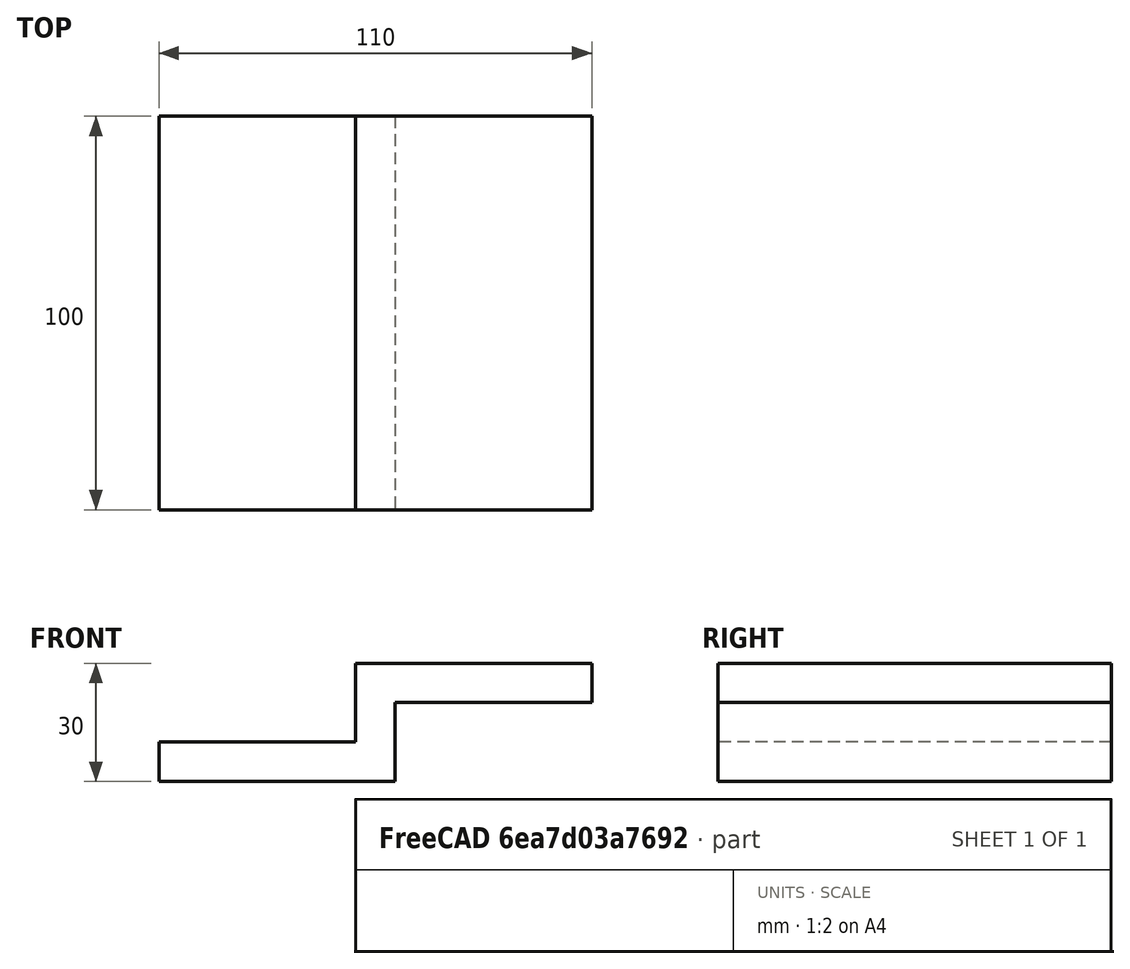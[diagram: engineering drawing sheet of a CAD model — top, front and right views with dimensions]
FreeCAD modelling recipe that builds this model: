
FCSTD DOCUMENT  (FreeCAD 0.17R13327 (Git))
Label: Z
License: All rights reserved
LicenseURL: http://en.wikipedia.org/wiki/All_rights_reserved
objects: Sketcher::SketchObject×1, PartDesign::Pad×1
note: 3 computed .brp shape members not serialized (recipe doc carries the construction recipe); baked Part::Feature solids carry a one-line shape summary decoded from their .brp

FEATURE [Sketcher::SketchObject] Sketch
  MapMode = 5
  Placement = pos=(0,0,0) rot=(1,0,0;1.5708rad)
  sketch-geometry (8):
    g0: LineSegment StartX=0 StartY=0 StartZ=0 EndX=60 EndY=0 EndZ=0
    g1: LineSegment StartX=60 StartY=0 StartZ=0 EndX=60 EndY=20 EndZ=0
    g2: LineSegment StartX=60 StartY=20 StartZ=0 EndX=110 EndY=20 EndZ=0
    g3: LineSegment StartX=110 StartY=20 StartZ=0 EndX=110 EndY=30 EndZ=0
    g4: LineSegment StartX=110 StartY=30 StartZ=0 EndX=50 EndY=30 EndZ=0
    g5: LineSegment StartX=50 StartY=30 StartZ=0 EndX=50 EndY=10 EndZ=0
    g6: LineSegment StartX=50 StartY=10 StartZ=0 EndX=0 EndY=10 EndZ=0
    g7: LineSegment StartX=0 StartY=10 StartZ=0 EndX=0 EndY=0 EndZ=0
  constraints (17):
    c: PointOnObject(g0,g-2)
    c: PointOnObject(g0,g-1)
    c: Horizontal(g0)
    c: Coincident(g0,g1)
    c: Vertical(g1)
    c: Coincident(g1,g2)
    c: Horizontal(g2)
    c: Coincident(g2,g3)
    c: Vertical(g3)
    c: Coincident(g3,g4)
    c: Horizontal(g4)
    c: Coincident(g4,g5)
    c: Vertical(g5)
    c: Horizontal(g6)
    c: Coincident(g6,g7)
    c: Coincident(g5,g6)
    c: Coincident(g-1,g7)
FEATURE [PartDesign::Pad] Pad
  Length = 100
  Length2 = 100
  Placement = pos=(0,0,0) rot=(1,0,0;1.5708rad)
  Profile = -> Sketch
  Type = 0
